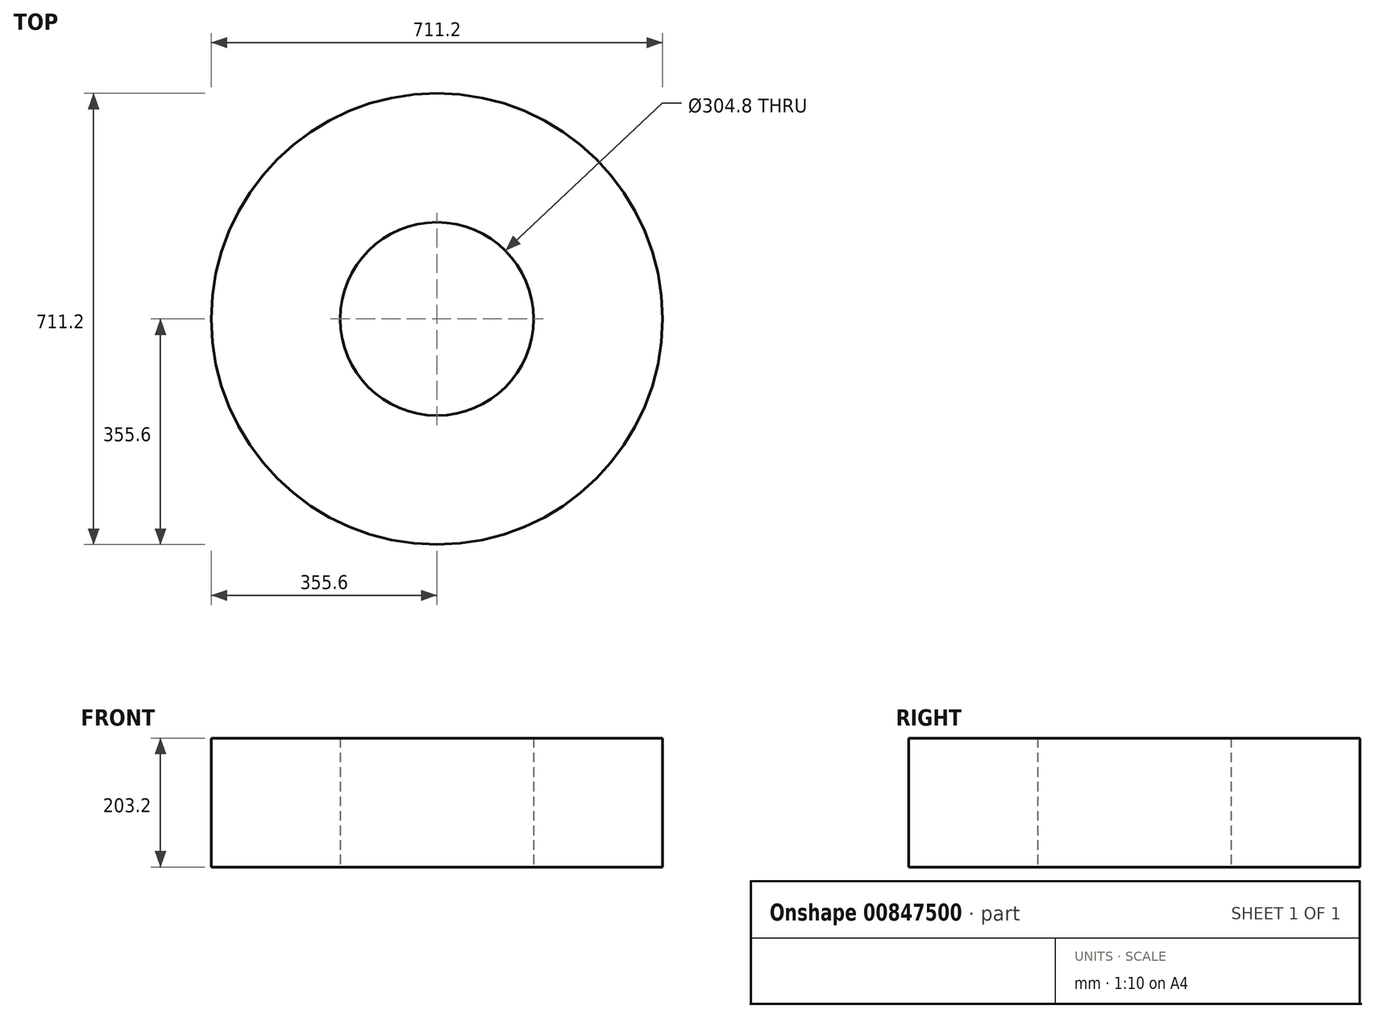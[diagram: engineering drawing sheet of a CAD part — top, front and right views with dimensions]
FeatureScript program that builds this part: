
annotation { "Feature Type Name" : "Feature", "Feature Type Description" : "" }
export const myFeature = defineFeature(function(context is Context, id is Id, definition is map)
    precondition{}
    {
        {
            var Q0;
            Q0=qCreatedBy(makeId("Top.planeOp"),FACE);
            var sketch = newSketch(context, id + "F0", { "sketchPlane" : qUnion([Q0])});
            skCircle(sketch, "E0", {"center": v(0, 0) * mm, "radius": 355.6 * mm});
            skCircle(sketch, "E1", {"center": v(0, 0) * mm, "radius": 152.4 * mm});
            skSolve(sketch);
        }
        {
            var Q0;
            Q0=makeQuery(id+"F0.imprint","IMPRINT",FACE,{"disambiguationData":[TD([[makeQuery(id+"F0.imprint","IMPRINT",EDGE,{"derivedFrom":sQuery(id+"F0.wireOp",EDGE,"E0")}),1.0]])]});
            extrude(context, id + "F1", {"entities" : qUnion([Q0]), "depth" : 203.2 * mm, "offsetDistance" : 25.4 * mm});
        }
    });
